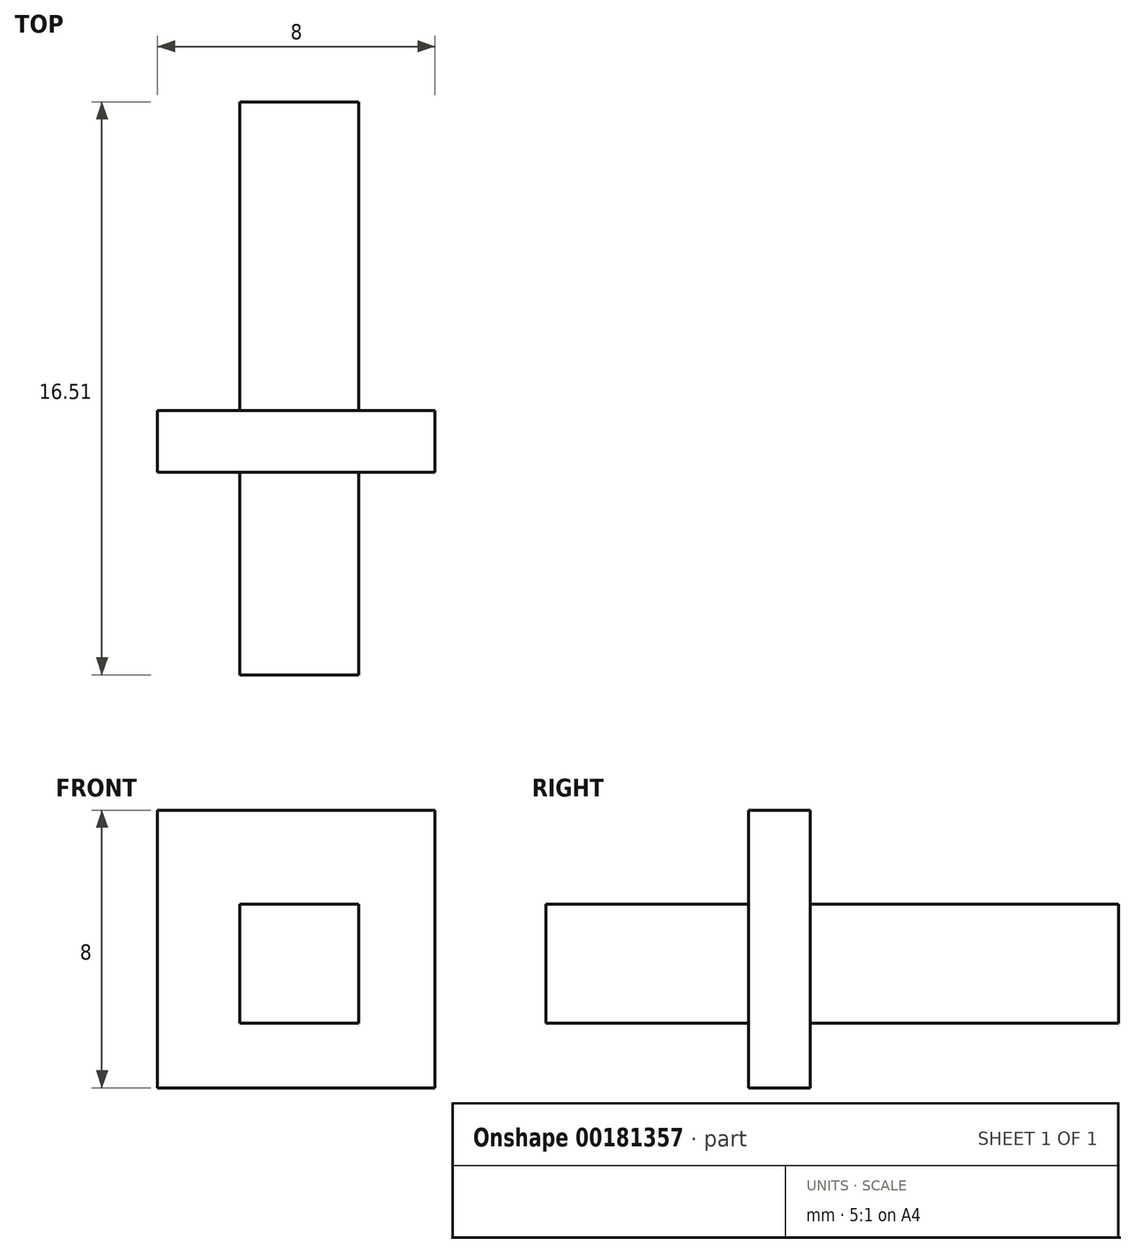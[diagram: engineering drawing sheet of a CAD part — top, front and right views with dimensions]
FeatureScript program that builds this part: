
annotation { "Feature Type Name" : "Feature", "Feature Type Description" : "" }
export const myFeature = defineFeature(function(context is Context, id is Id, definition is map)
    precondition{}
    {
        {
            var Q0;
            Q0=qCreatedBy(makeId("Front.planeOp"),FACE);
            var sketch = newSketch(context, id + "F0", { "sketchPlane" : qUnion([Q0])});
            skLineSegment(sketch, "E0.bottom", {"start": v(-56.16, 16.13) * mm, "end": v(-52.73, 16.13) * mm});
            skLineSegment(sketch, "E0.top", {"start": v(-56.16, 12.7) * mm, "end": v(-52.73, 12.7) * mm});
            skLineSegment(sketch, "E0.left", {"start": v(-56.16, 16.13) * mm, "end": v(-56.16, 12.7) * mm});
            skLineSegment(sketch, "E0.right", {"start": v(-52.73, 16.13) * mm, "end": v(-52.73, 12.7) * mm});
            skLineSegment(sketch, "E1.bottom", {"start": v(-58.53, 18.84) * mm, "end": v(-50.53, 18.84) * mm});
            skLineSegment(sketch, "E1.top", {"start": v(-58.53, 10.84) * mm, "end": v(-50.53, 10.84) * mm});
            skLineSegment(sketch, "E1.left", {"start": v(-58.53, 18.84) * mm, "end": v(-58.53, 10.84) * mm});
            skLineSegment(sketch, "E1.right", {"start": v(-50.53, 18.84) * mm, "end": v(-50.53, 10.84) * mm});
            skSolve(sketch);
        }
        {
            var Q0;
            Q0=makeQuery(id+"F0.imprint","IMPRINT",FACE,{"disambiguationData":[TD([[makeQuery(id+"F0.imprint","IMPRINT",EDGE,{"derivedFrom":sQuery(id+"F0.wireOp",EDGE,"E0.bottom")}),-1.0]])]});
            extrude(context, id + "F1", {"entities" : qUnion([Q0]), "depth" : 5.84 * mm, "hasSecondDirection" : true, "secondDirectionOppositeDirection" : true, "secondDirectionDepth" : 10.67 * mm});
        }
        {
            var Q0;
            Q0 = qSketchRegion(id + "F0", true);
            extrude(context, id + "F2", {"entities" : qUnion([Q0]), "operationType" : NewBodyOperationType.ADD, "oppositeDirection" : true, "depth" : 1.78 * mm});
        }
    });
